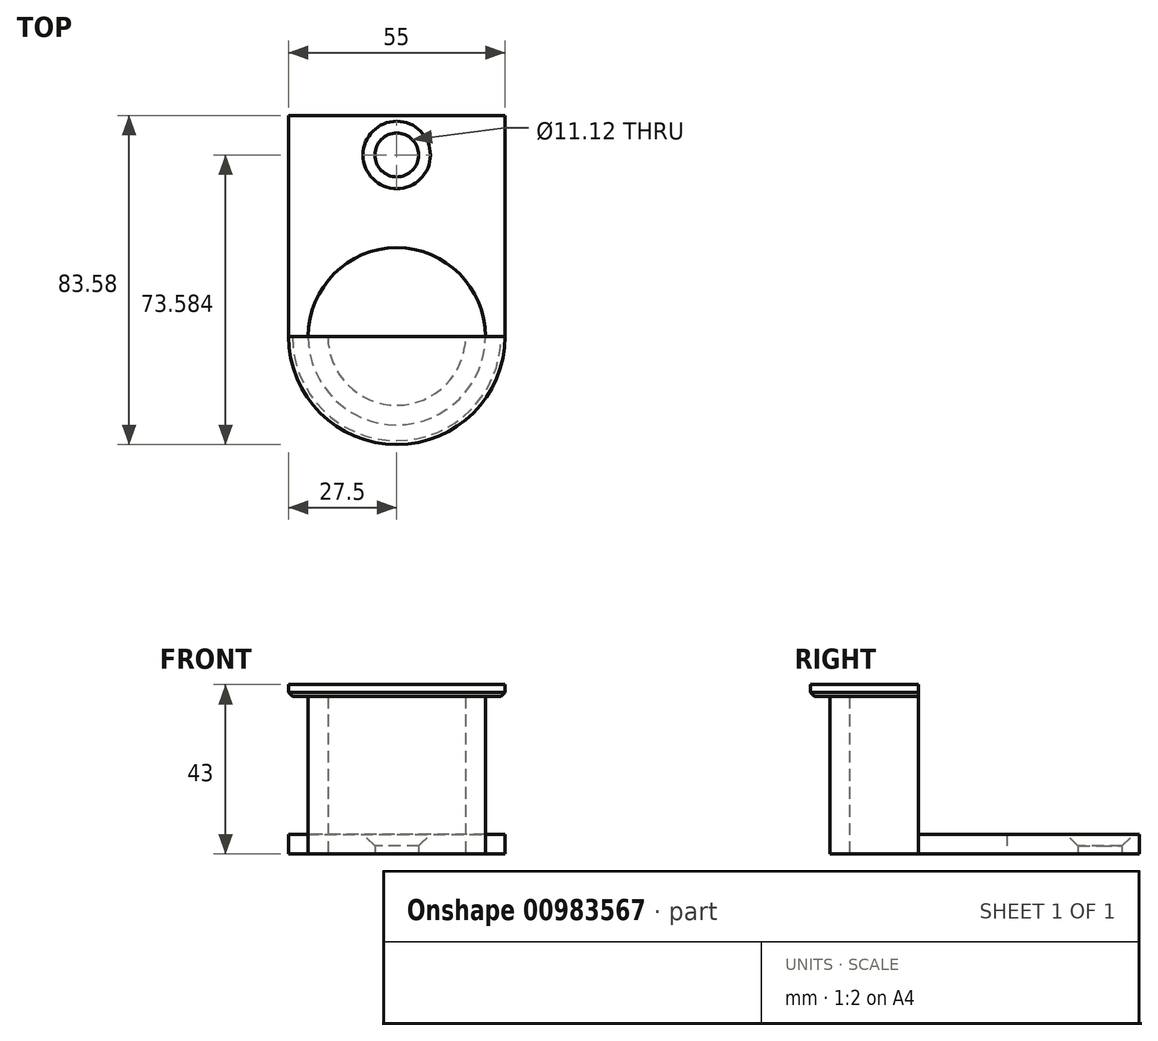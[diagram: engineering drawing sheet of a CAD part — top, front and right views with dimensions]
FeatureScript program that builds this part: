
annotation { "Feature Type Name" : "Feature", "Feature Type Description" : "" }
export const myFeature = defineFeature(function(context is Context, id is Id, definition is map)
    precondition{}
    {
        {
            var Q0;
            Q0=qCreatedBy(makeId("Top.planeOp"),FACE);
            var sketch = newSketch(context, id + "F0", { "sketchPlane" : qUnion([Q0])});
            skLineSegment(sketch, "E0.bottom", {"start": v(0, 56.08) * mm, "end": v(55, 56.08) * mm});
            skLineSegment(sketch, "E0.top", {"start": v(0, -56.08) * mm, "end": v(55, -56.08) * mm});
            skLineSegment(sketch, "E0.left", {"start": v(0, 56.08) * mm, "end": v(0, -56.08) * mm});
            skLineSegment(sketch, "E0.right", {"start": v(55, 56.08) * mm, "end": v(55, -56.08) * mm});
            skCircle(sketch, "E1", {"center": v(27.5, 0) * mm, "radius": 22.5 * mm});
            skLineSegment(sketch, "E2", {"start": v(0, 0) * mm, "end": v(55, 0) * mm});
            skCircle(sketch, "E3.0", {"center": v(27.5, 0) * mm, "radius": 17.5 * mm});
            skCircle(sketch, "E4", {"center": v(27.5, 46.08) * mm, "radius": 5.56 * mm});
            skLineSegment(sketch, "E5", {"start": v(0, 46.08) * mm, "end": v(55, 46.08) * mm});
            skSolve(sketch);
        }
        {
            var Q0;
            {var subQ5=sQuery(id+"F0.wireOp",EDGE,"E0.bottom");Q0=makeQuery(id+"F0.imprint","IMPRINT",FACE,{"disambiguationData":[TD([[makeQuery(id+"F0.imprint","IMPRINT",EDGE,{"derivedFrom":subQ5}),-1.0]])]});}
            var Q1;
            {var subQ0=sQuery(id+"F0.wireOp",EDGE,"E2");var subQ1=sQuery(id+"F0.wireOp",EDGE,"E0.left");var subQ2=makeQuery(id+"F0.imprint","INTERSECT",VERTEX,{"derivedFrom":[subQ1,subQ0]});Q1=makeQuery(id+"F0.imprint","IMPRINT",FACE,{"disambiguationData":[TD([[makeQuery(id+"F0.imprint","IMPRINT",EDGE,{"disambiguationData":[TD([[subQ2,1.0]])],"derivedFrom":subQ1}),1.0]])]});}
            extrude(context, id + "F1", {"entities" : qUnion([Q0, Q1]), "depth" : 5 * mm, "offsetDistance" : 25 * mm});
        }
        {
            var Q0;
            {var subQ0=sQuery(id+"F0.wireOp",EDGE,"E2");var subQ1=sQuery(id+"F0.wireOp",EDGE,"E1");var subQ2=makeQuery(id+"F0.imprint","INTERSECT",VERTEX,{"disambiguationData":[OD(0.0)],"derivedFrom":[subQ1,subQ0]});Q0=makeQuery(id+"F0.imprint","IMPRINT",FACE,{"disambiguationData":[TD([[makeQuery(id+"F0.imprint","IMPRINT",EDGE,{"disambiguationData":[TD([[subQ2,1.0]])],"derivedFrom":subQ1}),1.0]])]});}
            extrude(context, id + "F2", {"entities" : qUnion([Q0]), "operationType" : NewBodyOperationType.ADD, "depth" : 40 * mm, "offsetDistance" : 25 * mm});
        }
        {
            var Q0;
            Q0=makeQuery(id+"F1.opExtrude","CAP_EDGE",EDGE,{"disambiguationData":[OSD([sQuery(id+"F0.wireOp",EDGE,"E4")])],"isStart":false});
            chamfer(context, id + "F3", {"entities" : qUnion([Q0]), "width" : 3 * mm, "tangentPropagation" : true});
        }
        {
            var Q0;
            Q0=makeQuery(id+"F2.opExtrude","CAP_FACE",FACE,{"disambiguationData":[OSD([sQuery(id+"F0.wireOp",EDGE,"E1"),sQuery(id+"F0.wireOp",EDGE,"E2"),sQuery(id+"F0.wireOp",EDGE,"E3.0")])],"isStart":false});
            var sketch = newSketch(context, id + "F4", { "sketchPlane" : qUnion([Q0])});
            skCircle(sketch, "E6.0", {"center": v(27.5, 0) * mm, "radius": 27.5 * mm});
            skLineSegment(sketch, "E7", {"start": v(0, 0) * mm, "end": v(55, 0) * mm});
            skSolve(sketch);
        }
        {
            var Q0;
            {var subQ1=makeQuery(id+"F2.opExtrude","CAP_EDGE",EDGE,{"disambiguationData":[OSD([sQuery(id+"F0.wireOp",EDGE,"E3.0")])],"isStart":false});Q0=makeQuery(id+"F4.imprint","IMPRINT",FACE,{"disambiguationData":[TD([[makeQuery(id+"F4.imprint","IMPRINT",EDGE,{"derivedFrom":subQ1}),1.0]])]});}
            var Q1;
            {var subQ1=makeQuery(id+"F2.opExtrude","CAP_EDGE",EDGE,{"disambiguationData":[OSD([sQuery(id+"F0.wireOp",EDGE,"E1")])],"isStart":false});Q1=makeQuery(id+"F4.imprint","IMPRINT",FACE,{"disambiguationData":[TD([[makeQuery(id+"F4.imprint","IMPRINT",EDGE,{"derivedFrom":subQ1}),1.0]])]});}
            var Q2;
            {var subQ4=makeQuery(id+"F2.opExtrude","CAP_EDGE",EDGE,{"disambiguationData":[OSD([sQuery(id+"F0.wireOp",EDGE,"E1")])],"isStart":false});Q2=makeQuery(id+"F4.imprint","IMPRINT",FACE,{"disambiguationData":[TD([[makeQuery(id+"F4.imprint","IMPRINT",EDGE,{"derivedFrom":subQ4}),-1.0]])]});}
            extrude(context, id + "F5", {"entities" : qUnion([Q0, Q1, Q2]), "operationType" : NewBodyOperationType.ADD, "depth" : 3 * mm, "offsetDistance" : 25 * mm});
        }
        {
            var Q0;
            Q0=makeQuery(id+"F5.opExtrude","CAP_EDGE",EDGE,{"disambiguationData":[OSD([sQuery(id+"F4.wireOp",EDGE,"E6.0")])],"isStart":true});
            chamfer(context, id + "F6", {"entities" : qUnion([Q0]), "width" : 1 * mm, "tangentPropagation" : true});
        }
    });
